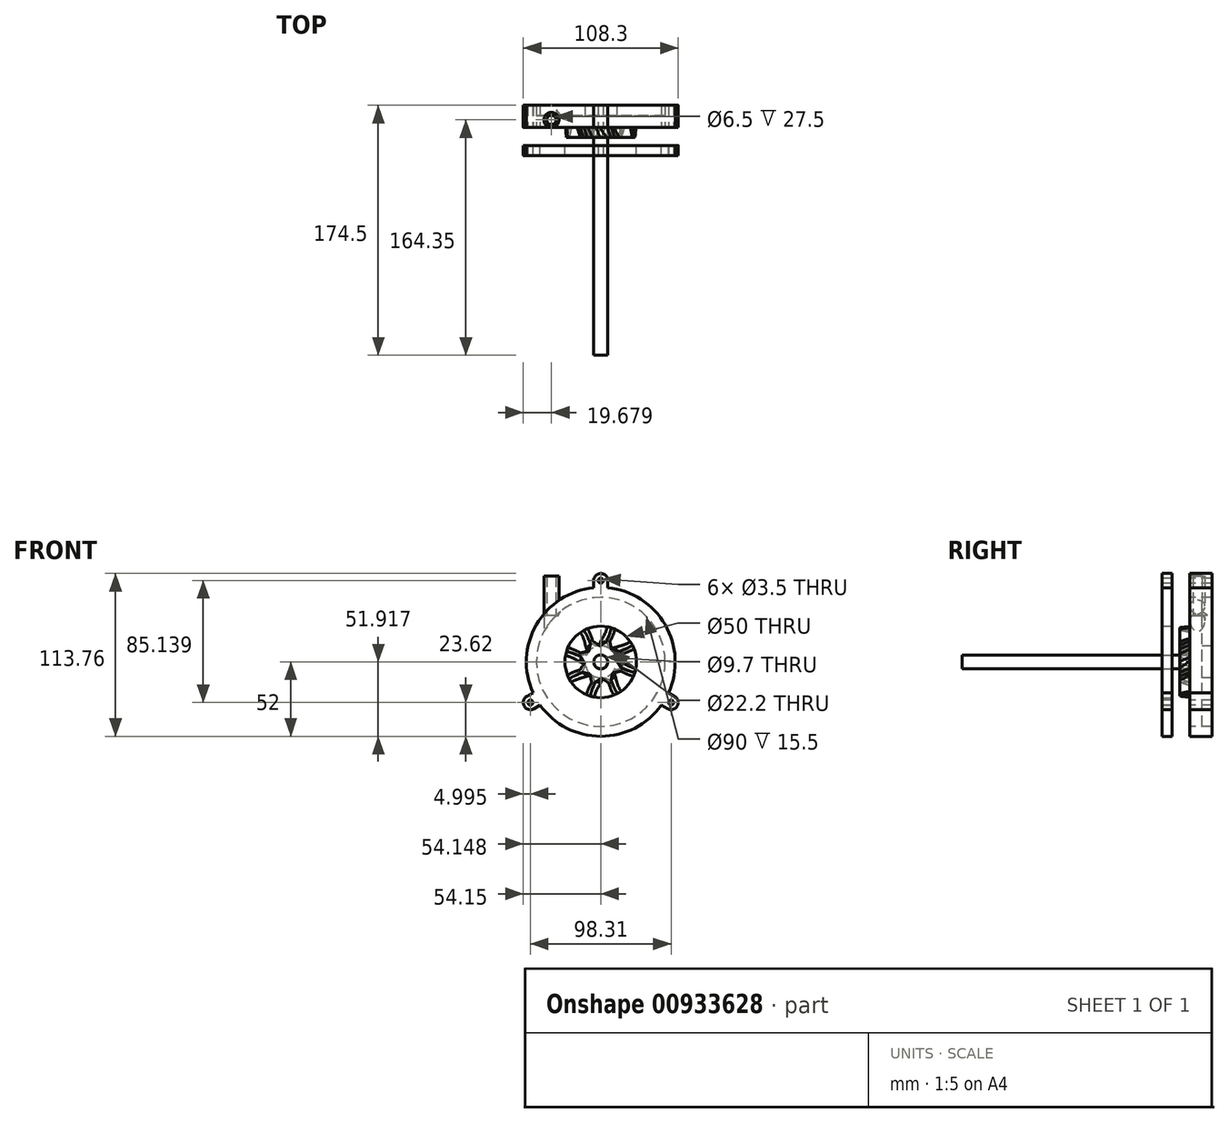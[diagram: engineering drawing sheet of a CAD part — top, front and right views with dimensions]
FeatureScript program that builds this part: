
annotation { "Feature Type Name" : "Feature", "Feature Type Description" : "" }
export const myFeature = defineFeature(function(context is Context, id is Id, definition is map)
    precondition{}
    {
        {
            var Q0;
            Q0=qCreatedBy(makeId("Front.planeOp"),FACE);
            var sketch = newSketch(context, id + "F0", { "sketchPlane" : qUnion([Q0])});
            skCircle(sketch, "E0", {"center": v(0, 0) * mm, "radius": 4.85 * mm});
            skCircle(sketch, "E1.0", {"center": v(0, 0) * mm, "radius": 10.85 * mm});
            skFitSpline(sketch, "E2", {"points": [v(-10.85, 0) * mm, v(-26.63, 6.23) * mm, v(-42.34, 0) * mm], "startDerivative": vector(-31.74, 18.78) * mm, "endDerivative": vector(-33.68, -18.59) * mm});
            skLineSegment(sketch, "E3", {"start": v(-42.34, 0) * mm, "end": v(-42.16, -2) * mm});
            skFitSpline(sketch, "E4", {"points": [v(-42.16, -2) * mm, v(-27.23, 3.48) * mm, v(-10.67, -2) * mm], "startDerivative": vector(30.43, 14.98) * mm, "endDerivative": vector(25.07, -11.68) * mm});
            skLineSegment(sketch, "E5", {"start": v(-10.85, 0) * mm, "end": v(-10.67, -2) * mm});
            skSolve(sketch);
        }
        {
            var Q0;
            Q0=qCreatedBy(makeId("Front.planeOp"),FACE);
            cPlane(context, id + "F1", {"entities" : qUnion([Q0]), "cplaneType" : CPlaneType.OFFSET, "offset" : 7 * mm, "width" : 150 * mm, "height" : 150 * mm});
        }
        {
            var Q0;
            Q0=qCreatedBy(makeId("Front.planeOp"),FACE);
            cPlane(context, id + "F2", {"entities" : qUnion([Q0]), "cplaneType" : CPlaneType.OFFSET, "offset" : 7 * mm, "oppositeDirection" : true, "width" : 150 * mm, "height" : 150 * mm});
        }
        {
            var Q0;
            Q0=qCreatedBy(id+"F1.planeOp",FACE);
            var sketch = newSketch(context, id + "F3", { "sketchPlane" : qUnion([Q0])});
            skCircle(sketch, "E6", {"center": v(0, -0.08) * mm, "radius": 4.85 * mm});
            skCircle(sketch, "E7.0", {"center": v(0, -0.08) * mm, "radius": 10.85 * mm});
            skFitSpline(sketch, "E8", {"points": [v(-10.08, 3.9) * mm, v(-25.87, 10.13) * mm, v(-41.58, 3.9) * mm], "startDerivative": vector(-31.74, 18.78) * mm, "endDerivative": vector(-33.68, -18.59) * mm});
            skLineSegment(sketch, "E9", {"start": v(-41.58, 3.9) * mm, "end": v(-41.4, 1.9) * mm});
            skFitSpline(sketch, "E10", {"points": [v(-41.4, 1.9) * mm, v(-26.46, 7.38) * mm, v(-9.9, 1.9) * mm], "startDerivative": vector(30.43, 14.98) * mm, "endDerivative": vector(25.07, -11.68) * mm});
            skLineSegment(sketch, "E11", {"start": v(-10.08, 3.9) * mm, "end": v(-9.9, 1.9) * mm});
            skSolve(sketch);
        }
        {
            var Q0;
            Q0=qCreatedBy(id+"F2.planeOp",FACE);
            var sketch = newSketch(context, id + "F4", { "sketchPlane" : qUnion([Q0])});
            skArc(sketch, "E12.0.0", {"start": v(-10.67, -2) * mm, "mid": v(10.8, 1) * mm, "end": v(-10.85, 0) * mm});
            skLineSegment(sketch, "E12.0.1", {"start": v(-8.48, -5) * mm, "end": v(-8.3, -7) * mm});
            skArc(sketch, "E12.1.0", {"start": v(-10.67, -2) * mm, "mid": v(-10.8, -1) * mm, "end": v(-10.85, 0) * mm});
            skFitSpline(sketch, "E12.1.1", {"points": [v(-8.48, -5) * mm, v(-13.78, -1.87) * mm, v(-24.44, 4.34) * mm, v(-34.37, -1.9) * mm, v(-39.98, -5) * mm]});
            skLineSegment(sketch, "E12.1.2", {"start": v(-39.98, -5) * mm, "end": v(-39.8, -7) * mm});
            skFitSpline(sketch, "E12.1.3", {"points": [v(-39.8, -7) * mm, v(-34.84, -4.55) * mm, v(-25.5, 1.73) * mm, v(-12.57, -5) * mm, v(-8.3, -7) * mm]});
            skSolve(sketch);
        }
        {
            var Q0;
            {var subQ5=sQuery(id+"F3.wireOp",EDGE,"E9");Q0=makeQuery(id+"F3.imprint","IMPRINT",FACE,{"disambiguationData":[TD([[makeQuery(id+"F3.imprint","IMPRINT",EDGE,{"derivedFrom":subQ5}),1.0]])]});}
            var Q1;
            {var subQ4=sQuery(id+"F4.wireOp",EDGE,"E12.1.2");Q1=makeQuery(id+"F4.imprint","IMPRINT",FACE,{"disambiguationData":[TD([[makeQuery(id+"F4.imprint","IMPRINT",EDGE,{"derivedFrom":subQ4}),1.0]])]});}
            loft(context, id + "F5", {"sheetProfilesArray" : [{ "sheetProfileEntities" : qUnion([Q0]) }, { "sheetProfileEntities" : qUnion([Q1]) }]});
        }
        {
            var Q0;
            Q0=makeQuery(id+"F3.imprint","IMPRINT",FACE,{"disambiguationData":[TD([[makeQuery(id+"F3.imprint","IMPRINT",EDGE,{"derivedFrom":sQuery(id+"F3.wireOp",EDGE,"E6")}),-1.0]])]});
            var Q1;
            {var subQ5=sQuery(id+"F3.wireOp",EDGE,"E11");Q1=makeQuery(id+"F3.imprint","IMPRINT",FACE,{"disambiguationData":[TD([[makeQuery(id+"F3.imprint","IMPRINT",EDGE,{"derivedFrom":subQ5}),-1.0]])]});}
            extrude(context, id + "F6", {"entities" : qUnion([Q0, Q1]), "operationType" : NewBodyOperationType.ADD, "oppositeDirection" : true, "depth" : 14 * mm, "offsetDistance" : 25 * mm});
        }
        {
            var Q0;
            {var subQ0=sQuery(id+"F3.wireOp",EDGE,"E7.0");Q0=makeQuery(id+"F6.boolean.opBoolean","INTERSECT",EDGE,{"derivedFrom":[makeQuery(id+"F5.opLoft","SWEPT_FACE",FACE,{"disambiguationData":[OSD([subQ0,sQuery(id+"F3.wireOp",EDGE,"E9"),sQuery(id+"F3.wireOp",EDGE,"E10"),sQuery(id+"F4.wireOp",EDGE,"E12.0.0"),sQuery(id+"F4.wireOp",EDGE,"E12.0.1"),sQuery(id+"F4.wireOp",EDGE,"E12.1.2"),sQuery(id+"F4.wireOp",EDGE,"E12.1.3")])]}),makeQuery(id+"F6.opExtrude","SWEPT_FACE",FACE,{"disambiguationData":[OSD([subQ0])]})]});}
            var Q1;
            {var subQ0=sQuery(id+"F3.wireOp",EDGE,"E7.0");Q1=makeQuery(id+"F6.boolean.opBoolean","INTERSECT",EDGE,{"derivedFrom":[makeQuery(id+"F5.opLoft","SWEPT_FACE",FACE,{"disambiguationData":[OSD([subQ0,sQuery(id+"F3.wireOp",EDGE,"E8"),sQuery(id+"F3.wireOp",EDGE,"E9"),sQuery(id+"F4.wireOp",EDGE,"E12.0.0"),sQuery(id+"F4.wireOp",EDGE,"E12.1.1"),sQuery(id+"F4.wireOp",EDGE,"E12.1.2")])]}),makeQuery(id+"F6.opExtrude","SWEPT_FACE",FACE,{"disambiguationData":[OSD([subQ0])]})]});}
            chamfer(context, id + "F7", {"entities" : qUnion([Q0, Q1]), "width" : 5 * mm, "tangentPropagation" : true});
        }
        {
            var Q0;
            {var subQ4=sQuery(id+"F4.wireOp",EDGE,"E12.1.2");var subQ10=sQuery(id+"F3.wireOp",EDGE,"E9");Q0=makeQuery(id+"F5.opLoft","SWEPT_BODY",BODY,{"disambiguationData":[OSD([makeQuery(id+"F3.imprint","IMPRINT",FACE,{"disambiguationData":[TD([[makeQuery(id+"F3.imprint","IMPRINT",EDGE,{"derivedFrom":subQ10}),1.0]])]}),makeQuery(id+"F4.imprint","IMPRINT",FACE,{"disambiguationData":[TD([[makeQuery(id+"F4.imprint","IMPRINT",EDGE,{"derivedFrom":subQ4}),1.0]])]})])]});}
            var Q1;
            Q1=makeQuery(id+"F6.opExtrude","CAP_EDGE",EDGE,{"disambiguationData":[OSD([sQuery(id+"F3.wireOp",EDGE,"E6")])],"isStart":true});
            circularPattern(context, id + "F8", {"operationType" : NewBodyOperationType.ADD, "entities" : qUnion([Q0]), "axis" : qUnion([Q1]), "angle" : 360 * degree, "instanceCount" : 8, "equalSpace" : true});
        }
        {
            var Q0;
            Q0=qCreatedBy(makeId("Front.planeOp"),FACE);
            var sketch = newSketch(context, id + "F9", { "sketchPlane" : qUnion([Q0])});
            skCircle(sketch, "E13", {"center": v(0, 0) * mm, "radius": 45 * mm});
            skCircle(sketch, "E14.0", {"center": v(0, 0) * mm, "radius": 52 * mm});
            skCircle(sketch, "E15", {"center": v(0, 0) * mm, "radius": 25 * mm});
            skCircle(sketch, "E16.0", {"center": v(0, 0) * mm, "radius": 44.7 * mm});
            skSolve(sketch);
        }
        {
            var Q0;
            Q0=makeQuery(id+"F9.imprint","IMPRINT",FACE,{"disambiguationData":[TD([[makeQuery(id+"F9.imprint","IMPRINT",EDGE,{"derivedFrom":sQuery(id+"F9.wireOp",EDGE,"E13")}),-1.0]])]});
            extrude(context, id + "F10", {"entities" : qUnion([Q0]), "oppositeDirection" : true, "depth" : 15.5 * mm, "offsetDistance" : 25 * mm, "hasSecondDirection" : true, "secondDirectionOppositeDirection" : false, "secondDirectionDepth" : 12.5 * mm});
        }
        {
            var Q0;
            Q0=qCreatedBy(makeId("Top.planeOp"),FACE);
            var sketch = newSketch(context, id + "F11", { "sketchPlane" : qUnion([Q0])});
            skCircle(sketch, "E17", {"center": v(-34.47, 5.35) * mm, "radius": 5.25 * mm});
            skCircle(sketch, "E18.0", {"center": v(-34.47, 5.35) * mm, "radius": 3.25 * mm});
            skSolve(sketch);
        }
        {
            var Q0;
            Q0=qSketchRegion(id+"F11",true);
            extrude(context, id + "F12", {"entities" : qUnion([Q0]), "operationType" : NewBodyOperationType.ADD, "depth" : 60 * mm, "offsetDistance" : 25 * mm});
        }
        {
            var Q0;
            Q0=qSketchRegion(id+"F11",true);
            extrude(context, id + "F13", {"entities" : qUnion([Q0]), "operationType" : NewBodyOperationType.REMOVE, "depth" : 32.5 * mm, "offsetDistance" : 25 * mm});
        }
        {
            var Q0;
            Q0=makeQuery(id+"F11.imprint","IMPRINT",FACE,{"disambiguationData":[TD([[makeQuery(id+"F11.imprint","IMPRINT",EDGE,{"derivedFrom":sQuery(id+"F11.wireOp",EDGE,"E18.0")}),1.0]])]});
            extrude(context, id + "F14", {"entities" : qUnion([Q0]), "operationType" : NewBodyOperationType.REMOVE, "depth" : 61.1 * mm, "offsetDistance" : 25 * mm});
        }
        {
            var Q0;
            {var subQ0=sQuery(id+"F11.wireOp",EDGE,"E17");Q0=makeQuery(id+"F13.boolean.opBoolean","COPY",EDGE,{"disambiguationData":[topologyDisambiguationEdgeConnected([makeQuery(id+"F12.opExtrude","SWEPT_FACE",FACE,{"disambiguationData":[OSD([subQ0])]})])],"derivedFrom":makeQuery(id+"F13.opExtrude","CAP_EDGE",EDGE,{"disambiguationData":[OSD([subQ0])],"isStart":false})});}
            fillet(context, id + "F15", {"entities" : qUnion([Q0]), "radius" : 1.5 * mm, "tangentPropagation" : true, "allowEdgeOverflow" : false});
        }
        {
            var Q0;
            {var subQ0=makeQuery(id+"F10.opExtrude","SWEPT_FACE",FACE,{"disambiguationData":[OSD([sQuery(id+"F9.wireOp",EDGE,"E13")])]});var subQ1=sQuery(id+"F11.wireOp",EDGE,"E17");Q0=makeQuery(id+"F13.boolean.opBoolean","SPLIT",EDGE,{"disambiguationData":[topologyDisambiguationEdgeConnected([makeQuery(id+"F13.opExtrude","SWEPT_FACE",FACE,{"disambiguationData":[OSD([subQ1])]})])],"derivedFrom":makeQuery(id+"F12.boolean.opBoolean","INTERSECT",EDGE,{"derivedFrom":[subQ0,makeQuery(id+"F12.opExtrude","SWEPT_FACE",FACE,{"disambiguationData":[OSD([subQ1])]})]})});}
            chamfer(context, id + "F16", {"entities" : qUnion([Q0]), "width" : 4 * mm, "tangentPropagation" : true});
        }
        {
            var Q0;
            Q0=qCreatedBy(makeId("Front.planeOp"),FACE);
            var sketch = newSketch(context, id + "F17", { "sketchPlane" : qUnion([Q0])});
            skCircle(sketch, "E19", {"center": v(0, 0) * mm, "radius": 4.85 * mm});
            skSolve(sketch);
        }
        {
            var Q0;
            Q0=makeQuery(id+"F17.imprint","IMPRINT",FACE,{"disambiguationData":[TD([[makeQuery(id+"F17.imprint","IMPRINT",EDGE,{"derivedFrom":sQuery(id+"F17.wireOp",EDGE,"E19")}),1.0]])]});
            extrude(context, id + "F18", {"entities" : qUnion([Q0]), "depth" : 159 * mm, "offsetDistance" : 25 * mm, "hasSecondDirection" : true, "secondDirectionOppositeDirection" : true, "secondDirectionDepth" : 15.5 * mm});
        }
        {
            var Q0;
            Q0=makeQuery(id+"F9.imprint","IMPRINT",FACE,{"disambiguationData":[TD([[makeQuery(id+"F9.imprint","IMPRINT",EDGE,{"derivedFrom":sQuery(id+"F9.wireOp",EDGE,"E15")}),-1.0]])]});
            var Q1;
            Q1=makeQuery(id+"F9.imprint","IMPRINT",FACE,{"disambiguationData":[TD([[makeQuery(id+"F9.imprint","IMPRINT",EDGE,{"derivedFrom":sQuery(id+"F9.wireOp",EDGE,"E13")}),1.0]])]});
            var Q2;
            Q2=makeQuery(id+"F9.imprint","IMPRINT",FACE,{"disambiguationData":[TD([[makeQuery(id+"F9.imprint","IMPRINT",EDGE,{"derivedFrom":sQuery(id+"F9.wireOp",EDGE,"E15")}),1.0]])]});
            extrude(context, id + "F19", {"entities" : qUnion([Q0, Q1, Q2]), "oppositeDirection" : true, "depth" : 15.5 * mm, "offsetDistance" : 25 * mm});
        }
        {
            var Q0;
            Q0=makeQuery(id+"F9.imprint","IMPRINT",FACE,{"disambiguationData":[TD([[makeQuery(id+"F9.imprint","IMPRINT",EDGE,{"derivedFrom":sQuery(id+"F9.wireOp",EDGE,"E15")}),-1.0]])]});
            var Q1;
            Q1=makeQuery(id+"F9.imprint","IMPRINT",FACE,{"disambiguationData":[TD([[makeQuery(id+"F9.imprint","IMPRINT",EDGE,{"derivedFrom":sQuery(id+"F9.wireOp",EDGE,"E13")}),1.0]])]});
            var Q2;
            Q2=makeQuery(id+"F9.imprint","IMPRINT",FACE,{"disambiguationData":[TD([[makeQuery(id+"F9.imprint","IMPRINT",EDGE,{"derivedFrom":sQuery(id+"F9.wireOp",EDGE,"E15")}),1.0]])]});
            extrude(context, id + "F20", {"entities" : qUnion([Q0, Q1, Q2]), "operationType" : NewBodyOperationType.REMOVE, "oppositeDirection" : true, "depth" : 8.5 * mm, "offsetDistance" : 25 * mm});
        }
        {
            var Q0;
            Q0=qCreatedBy(makeId("Front.planeOp"),FACE);
            var sketch = newSketch(context, id + "F21", { "sketchPlane" : qUnion([Q0])});
            skCircle(sketch, "E20", {"center": v(0, 0) * mm, "radius": 11.1 * mm});
            skSolve(sketch);
        }
        {
            var Q0;
            Q0=makeQuery(id+"F21.imprint","IMPRINT",FACE,{"disambiguationData":[TD([[makeQuery(id+"F21.imprint","IMPRINT",EDGE,{"derivedFrom":sQuery(id+"F21.wireOp",EDGE,"E20")}),1.0]])]});
            extrude(context, id + "F22", {"entities" : qUnion([Q0]), "operationType" : NewBodyOperationType.REMOVE, "oppositeDirection" : true, "depth" : 25 * mm, "offsetDistance" : 25 * mm});
        }
        {
            var Q0;
            Q0=makeQuery(id+"F9.imprint","IMPRINT",FACE,{"disambiguationData":[TD([[makeQuery(id+"F9.imprint","IMPRINT",EDGE,{"derivedFrom":sQuery(id+"F9.wireOp",EDGE,"E15")}),-1.0]])]});
            var Q1;
            Q1=makeQuery(id+"F9.imprint","IMPRINT",FACE,{"disambiguationData":[TD([[makeQuery(id+"F9.imprint","IMPRINT",EDGE,{"derivedFrom":sQuery(id+"F9.wireOp",EDGE,"E13")}),-1.0]])]});
            var Q2;
            Q2=makeQuery(id+"F9.imprint","IMPRINT",FACE,{"disambiguationData":[TD([[makeQuery(id+"F9.imprint","IMPRINT",EDGE,{"derivedFrom":sQuery(id+"F9.wireOp",EDGE,"E13")}),1.0]])]});
            extrude(context, id + "F23", {"entities" : qUnion([Q0, Q1, Q2]), "depth" : 19.5 * mm, "offsetDistance" : 25 * mm});
        }
        {
            var Q0;
            Q0=makeQuery(id+"F9.imprint","IMPRINT",FACE,{"disambiguationData":[TD([[makeQuery(id+"F9.imprint","IMPRINT",EDGE,{"derivedFrom":sQuery(id+"F9.wireOp",EDGE,"E15")}),-1.0]])]});
            var Q1;
            Q1=makeQuery(id+"F9.imprint","IMPRINT",FACE,{"disambiguationData":[TD([[makeQuery(id+"F9.imprint","IMPRINT",EDGE,{"derivedFrom":sQuery(id+"F9.wireOp",EDGE,"E13")}),1.0]])]});
            var Q2;
            Q2=makeQuery(id+"F9.imprint","IMPRINT",FACE,{"disambiguationData":[TD([[makeQuery(id+"F9.imprint","IMPRINT",EDGE,{"derivedFrom":sQuery(id+"F9.wireOp",EDGE,"E13")}),-1.0]])]});
            extrude(context, id + "F24", {"entities" : qUnion([Q0, Q1, Q2]), "operationType" : NewBodyOperationType.REMOVE, "depth" : 12.5 * mm, "offsetDistance" : 25 * mm});
        }
        {
            var Q0;
            Q0=qCreatedBy(makeId("Front.planeOp"),FACE);
            var sketch = newSketch(context, id + "F25", { "sketchPlane" : qUnion([Q0])});
            skCircle(sketch, "E21", {"center": v(0, 0) * mm, "radius": 52 * mm});
            skLineSegment(sketch, "E22.bottom", {"start": v(0, 61.76) * mm, "end": v(0, 61.76) * mm});
            skLineSegment(sketch, "E22.top", {"start": v(5, 51.76) * mm, "end": v(-5, 51.76) * mm});
            skLineSegment(sketch, "E22.left", {"start": v(5, 56.76) * mm, "end": v(5, 51.76) * mm});
            skLineSegment(sketch, "E22.right", {"start": v(-5, 56.76) * mm, "end": v(-5, 51.76) * mm});
            skPoint(sketch, "E22.middle", {"position": v(0, 52) * mm});
            skCircle(sketch, "E23", {"center": v(0, 56.76) * mm, "radius": 1.75 * mm});
            skPoint(sketch, "E24.visualSharp", {"position": v(-5, 61.76) * mm});
            skArc(sketch, "E24.filletArc", {"start": v(0, 61.76) * mm, "mid": v(-3.54, 60.3) * mm, "end": v(-5, 56.76) * mm});
            skPoint(sketch, "E25.visualSharp", {"position": v(5, 61.76) * mm});
            skArc(sketch, "E25.filletArc", {"start": v(5, 56.76) * mm, "mid": v(3.54, 60.3) * mm, "end": v(0, 61.76) * mm});
            skArc(sketch, "E26.1.0", {"start": v(-53.48, -30.88) * mm, "mid": v(-50.45, -33.2) * mm, "end": v(-46.65, -32.7) * mm});
            skLineSegment(sketch, "E26.1.1", {"start": v(-46.65, -32.7) * mm, "end": v(-42.32, -30.2) * mm});
            skLineSegment(sketch, "E26.1.2", {"start": v(-47.32, -21.55) * mm, "end": v(-42.32, -30.2) * mm});
            skLineSegment(sketch, "E26.1.3", {"start": v(-51.65, -24.05) * mm, "end": v(-47.32, -21.55) * mm});
            skArc(sketch, "E26.1.4", {"start": v(-51.65, -24.05) * mm, "mid": v(-53.98, -27.09) * mm, "end": v(-53.48, -30.88) * mm});
            skCircle(sketch, "E26.1.5", {"center": v(-49.15, -28.38) * mm, "radius": 1.75 * mm});
            skArc(sketch, "E26.2.0", {"start": v(53.48, -30.88) * mm, "mid": v(53.98, -27.09) * mm, "end": v(51.65, -24.05) * mm});
            skLineSegment(sketch, "E26.2.1", {"start": v(51.65, -24.05) * mm, "end": v(47.32, -21.55) * mm});
            skLineSegment(sketch, "E26.2.2", {"start": v(42.32, -30.2) * mm, "end": v(47.32, -21.55) * mm});
            skLineSegment(sketch, "E26.2.3", {"start": v(46.65, -32.7) * mm, "end": v(42.32, -30.2) * mm});
            skArc(sketch, "E26.2.4", {"start": v(46.65, -32.7) * mm, "mid": v(50.45, -33.2) * mm, "end": v(53.48, -30.88) * mm});
            skCircle(sketch, "E26.2.5", {"center": v(49.15, -28.38) * mm, "radius": 1.75 * mm});
            skSolve(sketch);
        }
        {
            var Q0;
            Q0=makeQuery(id+"F25.imprint","IMPRINT",FACE,{"disambiguationData":[TD([[makeQuery(id+"F25.imprint","IMPRINT",EDGE,{"derivedFrom":sQuery(id+"F25.wireOp",EDGE,"E26.1.0")}),1.0]])]});
            var Q1;
            {var subQ1=sQuery(id+"F25.wireOp",EDGE,"E22.left");Q1=makeQuery(id+"F25.imprint","IMPRINT",FACE,{"disambiguationData":[TD([[makeQuery(id+"F25.imprint","IMPRINT",EDGE,{"derivedFrom":subQ1}),-1.0]])]});}
            var Q2;
            Q2=makeQuery(id+"F25.imprint","IMPRINT",FACE,{"disambiguationData":[TD([[makeQuery(id+"F25.imprint","IMPRINT",EDGE,{"derivedFrom":sQuery(id+"F25.wireOp",EDGE,"E26.2.0")}),1.0]])]});
            extrude(context, id + "F26", {"entities" : qUnion([Q0, Q1, Q2]), "operationType" : NewBodyOperationType.ADD, "oppositeDirection" : true, "depth" : 15.5 * mm, "offsetDistance" : 25 * mm, "hasSecondDirection" : true, "secondDirectionOppositeDirection" : false, "secondDirectionDepth" : 12 * mm});
        }
        {
            var Q0;
            Q0=makeQuery(id+"F25.imprint","IMPRINT",FACE,{"disambiguationData":[TD([[makeQuery(id+"F25.imprint","IMPRINT",EDGE,{"derivedFrom":sQuery(id+"F25.wireOp",EDGE,"E26.1.0")}),1.0]])]});
            var Q1;
            {var subQ1=sQuery(id+"F25.wireOp",EDGE,"E22.left");Q1=makeQuery(id+"F25.imprint","IMPRINT",FACE,{"disambiguationData":[TD([[makeQuery(id+"F25.imprint","IMPRINT",EDGE,{"derivedFrom":subQ1}),-1.0]])]});}
            var Q2;
            Q2=makeQuery(id+"F25.imprint","IMPRINT",FACE,{"disambiguationData":[TD([[makeQuery(id+"F25.imprint","IMPRINT",EDGE,{"derivedFrom":sQuery(id+"F25.wireOp",EDGE,"E26.2.0")}),1.0]])]});
            extrude(context, id + "F27", {"entities" : qUnion([Q0, Q1, Q2]), "operationType" : NewBodyOperationType.ADD, "depth" : 19.5 * mm, "offsetDistance" : 25 * mm});
        }
        {
            var Q0;
            Q0=makeQuery(id+"F25.imprint","IMPRINT",FACE,{"disambiguationData":[TD([[makeQuery(id+"F25.imprint","IMPRINT",EDGE,{"derivedFrom":sQuery(id+"F25.wireOp",EDGE,"E26.1.0")}),1.0]])]});
            var Q1;
            Q1=makeQuery(id+"F25.imprint","IMPRINT",FACE,{"disambiguationData":[TD([[makeQuery(id+"F25.imprint","IMPRINT",EDGE,{"derivedFrom":sQuery(id+"F25.wireOp",EDGE,"E26.2.0")}),1.0]])]});
            var Q2;
            {var subQ1=sQuery(id+"F25.wireOp",EDGE,"E22.left");Q2=makeQuery(id+"F25.imprint","IMPRINT",FACE,{"disambiguationData":[TD([[makeQuery(id+"F25.imprint","IMPRINT",EDGE,{"derivedFrom":subQ1}),-1.0]])]});}
            extrude(context, id + "F28", {"entities" : qUnion([Q0, Q1, Q2]), "operationType" : NewBodyOperationType.REMOVE, "depth" : 12.5 * mm, "offsetDistance" : 25 * mm});
        }
    });
